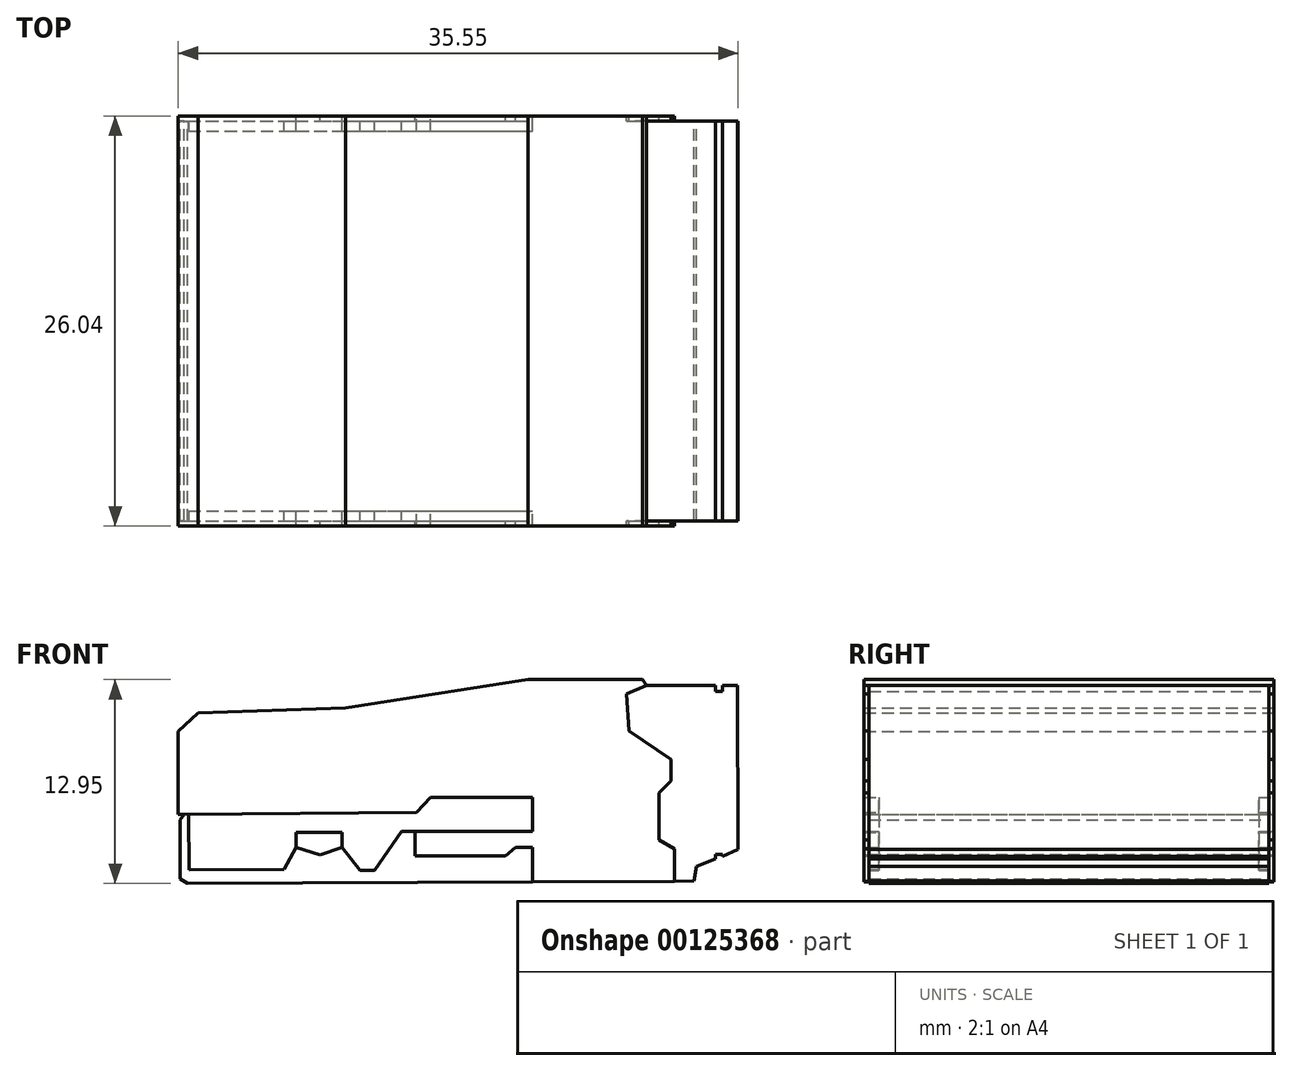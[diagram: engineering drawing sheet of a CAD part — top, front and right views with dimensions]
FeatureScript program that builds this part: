
annotation { "Feature Type Name" : "Feature", "Feature Type Description" : "" }
export const myFeature = defineFeature(function(context is Context, id is Id, definition is map)
    precondition{}
    {
        {
            var Q0;
            Q0=qCreatedBy(makeId("Front.planeOp"),FACE);
            var sketch = newSketch(context, id + "F0", { "sketchPlane" : qUnion([Q0])});
            skLineSegment(sketch, "E0", {"start": v(28.04, 12.43) * mm, "end": v(27.1, 12.43) * mm});
            skLineSegment(sketch, "E1", {"start": v(27.1, 12.43) * mm, "end": v(27.1, 12.05) * mm});
            skLineSegment(sketch, "E2", {"start": v(27.1, 12.05) * mm, "end": v(26.66, 12.05) * mm});
            skLineSegment(sketch, "E3", {"start": v(26.66, 12.05) * mm, "end": v(26.66, 12.43) * mm});
            skLineSegment(sketch, "E4", {"start": v(26.66, 12.43) * mm, "end": v(22.28, 12.43) * mm});
            skLineSegment(sketch, "E5", {"start": v(22.28, 12.43) * mm, "end": v(22, 12.8) * mm});
            skLineSegment(sketch, "E6", {"start": v(22, 12.8) * mm, "end": v(14.74, 12.8) * mm});
            skLineSegment(sketch, "E7", {"start": v(14.74, 12.8) * mm, "end": v(3.16, 11) * mm});
            skLineSegment(sketch, "E8", {"start": v(3.16, 11) * mm, "end": v(-6.22, 10.7) * mm});
            skLineSegment(sketch, "E9", {"start": v(-6.22, 10.7) * mm, "end": v(-7.47, 9.5) * mm});
            skLineSegment(sketch, "E10", {"start": v(-7.47, 9.5) * mm, "end": v(-7.47, 4.24) * mm});
            skLineSegment(sketch, "E11", {"start": v(-7.47, 4.24) * mm, "end": v(-7.1, 4.24) * mm});
            skLineSegment(sketch, "E12", {"start": v(-7.1, 4.24) * mm, "end": v(-7.35, 3.87) * mm});
            skLineSegment(sketch, "E13", {"start": v(-7.35, 3.87) * mm, "end": v(-7.35, 0.15) * mm});
            skLineSegment(sketch, "E14", {"start": v(-7.35, 0.15) * mm, "end": v(-6.88, -0.15) * mm});
            skLineSegment(sketch, "E15", {"start": v(-6.88, -0.15) * mm, "end": v(25.29, 0) * mm});
            skLineSegment(sketch, "E16", {"start": v(25.29, 0) * mm, "end": v(25.43, 0.93) * mm});
            skLineSegment(sketch, "E17", {"start": v(25.43, 0.93) * mm, "end": v(26.65, 1.41) * mm});
            skLineSegment(sketch, "E18", {"start": v(26.65, 1.41) * mm, "end": v(26.65, 1.7) * mm});
            skLineSegment(sketch, "E19", {"start": v(26.65, 1.7) * mm, "end": v(27.1, 1.7) * mm});
            skLineSegment(sketch, "E20", {"start": v(27.1, 1.7) * mm, "end": v(27.1, 1.57) * mm});
            skLineSegment(sketch, "E21", {"start": v(27.1, 1.57) * mm, "end": v(28.08, 2.01) * mm});
            skLineSegment(sketch, "E22", {"start": v(28.08, 2.01) * mm, "end": v(28.04, 12.43) * mm});
            skLineSegment(sketch, "E23", {"start": v(22.28, 12.43) * mm, "end": v(20.98, 11.9) * mm});
            skLineSegment(sketch, "E24", {"start": v(20.98, 11.9) * mm, "end": v(21.15, 9.53) * mm});
            skLineSegment(sketch, "E25", {"start": v(21.15, 9.53) * mm, "end": v(23.82, 7.74) * mm});
            skLineSegment(sketch, "E26", {"start": v(23.82, 7.74) * mm, "end": v(23.82, 6.36) * mm});
            skLineSegment(sketch, "E27", {"start": v(23.82, 6.36) * mm, "end": v(23.06, 5.6) * mm});
            skLineSegment(sketch, "E28", {"start": v(23.06, 5.6) * mm, "end": v(23.06, 2.62) * mm});
            skLineSegment(sketch, "E29", {"start": v(23.06, 2.62) * mm, "end": v(24.04, 2.04) * mm});
            skLineSegment(sketch, "E30", {"start": v(24.04, 2.04) * mm, "end": v(24.04, 0) * mm});
            skLineSegment(sketch, "E31", {"start": v(-7.1, 4.24) * mm, "end": v(7.66, 4.37) * mm});
            skLineSegment(sketch, "E32", {"start": v(7.66, 4.37) * mm, "end": v(8.56, 5.3) * mm});
            skLineSegment(sketch, "E33", {"start": v(8.56, 5.3) * mm, "end": v(15.02, 5.3) * mm});
            skLineSegment(sketch, "E34", {"start": v(15.02, 5.3) * mm, "end": v(15.02, -0.05) * mm});
            skLineSegment(sketch, "E35", {"start": v(-6.82, 4.25) * mm, "end": v(-6.8, 0.7) * mm});
            skLineSegment(sketch, "E36", {"start": v(-6.8, 0.7) * mm, "end": v(-0.74, 0.75) * mm});
            skLineSegment(sketch, "E37", {"start": v(-0.74, 0.75) * mm, "end": v(0, 2.14) * mm});
            skLineSegment(sketch, "E38", {"start": v(0, 2.14) * mm, "end": v(0, 3.08) * mm});
            skLineSegment(sketch, "E39", {"start": v(0, 3.08) * mm, "end": v(2.92, 3.08) * mm});
            skLineSegment(sketch, "E40", {"start": v(2.92, 3.08) * mm, "end": v(2.92, 2.14) * mm});
            skLineSegment(sketch, "E41", {"start": v(2.92, 2.14) * mm, "end": v(4.06, 0.68) * mm});
            skLineSegment(sketch, "E42", {"start": v(4.06, 0.68) * mm, "end": v(5, 0.68) * mm});
            skLineSegment(sketch, "E43", {"start": v(5, 0.68) * mm, "end": v(6.72, 3.14) * mm});
            skLineSegment(sketch, "E44", {"start": v(6.72, 3.14) * mm, "end": v(15.02, 3.14) * mm});
            skLineSegment(sketch, "E45", {"start": v(7.58, 3.14) * mm, "end": v(7.58, 1.58) * mm});
            skLineSegment(sketch, "E46", {"start": v(7.58, 1.58) * mm, "end": v(13.32, 1.58) * mm});
            skLineSegment(sketch, "E47", {"start": v(13.32, 1.58) * mm, "end": v(13.96, 2.14) * mm});
            skLineSegment(sketch, "E48", {"start": v(13.96, 2.14) * mm, "end": v(15.02, 2.14) * mm});
            skLineSegment(sketch, "E49", {"start": v(0, 2.14) * mm, "end": v(1.53, 1.68) * mm});
            skLineSegment(sketch, "E50", {"start": v(1.53, 1.68) * mm, "end": v(2.92, 2.14) * mm});
            skLineSegment(sketch, "E51", {"start": v(4.6, 4.34) * mm, "end": v(4.59, 5.33) * mm});
            skLineSegment(sketch, "E52", {"start": v(4.59, 5.33) * mm, "end": v(2.97, 5.9) * mm});
            skLineSegment(sketch, "E53", {"start": v(2.97, 5.9) * mm, "end": v(1.8, 5.3) * mm});
            skLineSegment(sketch, "E54", {"start": v(1.8, 5.3) * mm, "end": v(1.8, 4.32) * mm});
            skSolve(sketch);
        }
        {
            var Q0;
            Q0=makeQuery(id+"F0.imprint","IMPRINT",FACE,{"disambiguationData":[TD([[makeQuery(id+"F0.imprint","IMPRINT",EDGE,{"derivedFrom":sQuery(id+"F0.wireOp",EDGE,"E0")}),1.0]])]});
            extrude(context, id + "F1", {"entities" : qUnion([Q0]), "endBound" : BoundingType.SYMMETRIC, "depth" : 25.4 * mm});
        }
        {
            var Q0;
            Q0=makeQuery(id+"F0.imprint","IMPRINT",FACE,{"disambiguationData":[TD([[makeQuery(id+"F0.imprint","IMPRINT",EDGE,{"derivedFrom":sQuery(id+"F0.wireOp",EDGE,"E5")}),1.0]])]});
            extrude(context, id + "F2", {"entities" : qUnion([Q0]), "operationType" : NewBodyOperationType.ADD, "endBound" : BoundingType.SYMMETRIC, "depth" : 26.03 * mm});
        }
        {
            var Q0;
            {var subQ10=sQuery(id+"F0.wireOp",EDGE,"E32");Q0=makeQuery(id+"F0.imprint","IMPRINT",FACE,{"disambiguationData":[TD([[makeQuery(id+"F0.imprint","IMPRINT",EDGE,{"derivedFrom":subQ10}),-1.0]])]});}
            extrude(context, id + "F3", {"entities" : qUnion([Q0]), "operationType" : NewBodyOperationType.ADD, "endBound" : BoundingType.SYMMETRIC, "depth" : 24.13 * mm});
        }
        {
            var Q0;
            {var subQ4=sQuery(id+"F0.wireOp",EDGE,"E45");Q0=makeQuery(id+"F0.imprint","IMPRINT",FACE,{"disambiguationData":[TD([[makeQuery(id+"F0.imprint","IMPRINT",EDGE,{"derivedFrom":subQ4}),1.0]])]});}
            var Q1;
            Q1=makeQuery(id+"F0.imprint","IMPRINT",FACE,{"disambiguationData":[TD([[makeQuery(id+"F0.imprint","IMPRINT",EDGE,{"derivedFrom":sQuery(id+"F0.wireOp",EDGE,"E38")}),-1.0]])]});
            extrude(context, id + "F4", {"entities" : qUnion([Q0, Q1]), "operationType" : NewBodyOperationType.ADD, "endBound" : BoundingType.SYMMETRIC, "depth" : 26.03 * mm});
        }
        {
            var Q0;
            {var subQ0=sQuery(id+"F0.wireOp",EDGE,"E51");Q0=makeQuery(id+"F0.imprint","IMPRINT",FACE,{"disambiguationData":[TD([[makeQuery(id+"F0.imprint","IMPRINT",EDGE,{"derivedFrom":subQ0}),1.0]])]});}
            extrude(context, id + "F5", {"entities" : qUnion([Q0]), "operationType" : NewBodyOperationType.ADD, "endBound" : BoundingType.SYMMETRIC, "depth" : 26.03 * mm});
        }
        {
            var Q0;
            {var subQ2=sQuery(id+"F0.wireOp",EDGE,"E12");Q0=makeQuery(id+"F0.imprint","IMPRINT",FACE,{"disambiguationData":[TD([[makeQuery(id+"F0.imprint","IMPRINT",EDGE,{"derivedFrom":subQ2}),1.0]])]});}
            extrude(context, id + "F6", {"entities" : qUnion([Q0]), "operationType" : NewBodyOperationType.ADD, "endBound" : BoundingType.SYMMETRIC, "depth" : 25.4 * mm});
        }
    });
